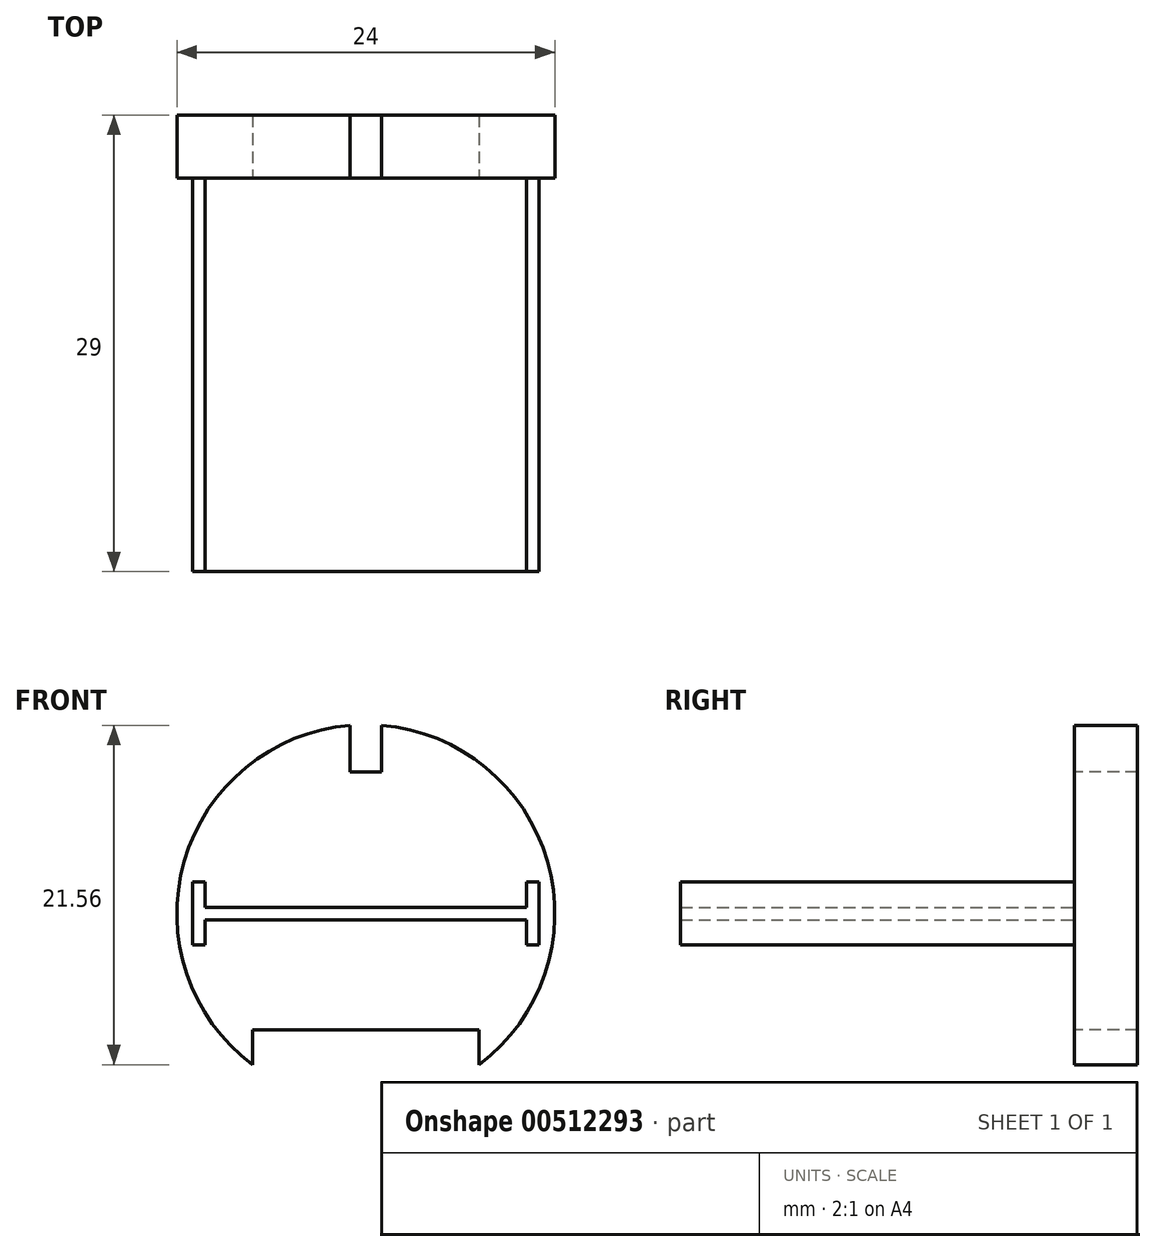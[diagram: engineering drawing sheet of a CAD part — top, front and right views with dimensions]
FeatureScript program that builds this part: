
annotation { "Feature Type Name" : "Feature", "Feature Type Description" : "" }
export const myFeature = defineFeature(function(context is Context, id is Id, definition is map)
    precondition{}
    {
        {
            var Q0;
            Q0=qCreatedBy(makeId("Front.planeOp"),FACE);
            var sketch = newSketch(context, id + "F0", { "sketchPlane" : qUnion([Q0])});
            skLineSegment(sketch, "E0.bottom", {"start": v(-10.2, 0.4) * mm, "end": v(10.2, 0.4) * mm});
            skLineSegment(sketch, "E0.top", {"start": v(-10.2, -0.4) * mm, "end": v(10.2, -0.4) * mm});
            skLineSegment(sketch, "E1", {"start": v(0, 0) * mm, "end": v(0, 72.24) * mm, "construction": true});
            skLineSegment(sketch, "E2", {"start": v(-29.5, 0) * mm, "end": v(0, 0) * mm, "construction": true});
            skLineSegment(sketch, "E3.bottom", {"start": v(-11, 2) * mm, "end": v(-10.2, 2) * mm});
            skLineSegment(sketch, "E3.top", {"start": v(-11, -2) * mm, "end": v(-10.2, -2) * mm});
            skLineSegment(sketch, "E3.left", {"start": v(-11, 2) * mm, "end": v(-11, -2) * mm});
            skLineSegment(sketch, "E3.right", {"start": v(-10.2, 2) * mm, "end": v(-10.2, 0.4) * mm});
            skLineSegment(sketch, "E4.bottom", {"start": v(11, 2) * mm, "end": v(10.2, 2) * mm});
            skLineSegment(sketch, "E4.top", {"start": v(11, -2) * mm, "end": v(10.2, -2) * mm});
            skLineSegment(sketch, "E4.left", {"start": v(11, 2) * mm, "end": v(11, -2) * mm});
            skLineSegment(sketch, "E4.right", {"start": v(10.2, 2) * mm, "end": v(10.2, 0.4) * mm});
            skLineSegment(sketch, "E5.trimOffspring", {"start": v(-10.2, -0.4) * mm, "end": v(-10.2, -2) * mm});
            skLineSegment(sketch, "E6.trimOffspring", {"start": v(10.2, -0.4) * mm, "end": v(10.2, -2) * mm});
            skPoint(sketch, "E7.trimOffspring.start.orphan", {"position": v(11, -0.4) * mm});
            skPoint(sketch, "E8.orphan", {"position": v(-11, 0.4) * mm});
            skLineSegment(sketch, "E9", {"start": v(10.2, -2) * mm, "end": v(-10.2, -2) * mm, "construction": true});
            skLineSegment(sketch, "E10", {"start": v(-10.2, 2) * mm, "end": v(10.2, 2) * mm, "construction": true});
            skSolve(sketch);
        }
        {
            var Q0;
            Q0=qCreatedBy(makeId("Front.planeOp"),FACE);
            var sketch = newSketch(context, id + "F1", { "sketchPlane" : qUnion([Q0])});
            skCircle(sketch, "E11", {"center": v(0, 0) * mm, "radius": 12 * mm});
            skSolve(sketch);
        }
        {
            var Q0;
            Q0 = qSketchRegion(id + "F1", true);
            extrude(context, id + "F2", {"entities" : qUnion([Q0]), "oppositeDirection" : true, "depth" : 4 * mm, "offsetDistance" : 25 * mm});
        }
        {
            var Q0;
            Q0 = qSketchRegion(id + "F0", true);
            extrude(context, id + "F3", {"entities" : qUnion([Q0]), "operationType" : NewBodyOperationType.ADD, "depth" : 25 * mm, "offsetDistance" : 25 * mm});
        }
        {
            var Q0;
            Q0=makeQuery(id+"F2.opExtrude","CAP_FACE",FACE,{"disambiguationData":[OSD([sQuery(id+"F1.wireOp",EDGE,"E11")])],"isStart":true});
            var sketch = newSketch(context, id + "F4", { "sketchPlane" : qUnion([Q0])});
            skLineSegment(sketch, "E12.bottom", {"start": v(-1, 14.62) * mm, "end": v(1, 14.62) * mm});
            skLineSegment(sketch, "E12.top", {"start": v(-1, 9) * mm, "end": v(1, 9) * mm});
            skLineSegment(sketch, "E12.left", {"start": v(-1, 14.62) * mm, "end": v(-1, 9) * mm});
            skLineSegment(sketch, "E12.right", {"start": v(1, 14.62) * mm, "end": v(1, 9) * mm});
            skLineSegment(sketch, "E13", {"start": v(0, 0) * mm, "end": v(0, 12) * mm, "construction": true});
            skLineSegment(sketch, "E14", {"start": v(-12, 0) * mm, "end": v(12, 0) * mm, "construction": true});
            skLineSegment(sketch, "E15.bottom", {"start": v(-7.2, -7.4) * mm, "end": v(7.2, -7.4) * mm});
            skLineSegment(sketch, "E15.top", {"start": v(-7.2, -17.4) * mm, "end": v(7.2, -17.4) * mm});
            skLineSegment(sketch, "E15.left", {"start": v(-7.2, -7.4) * mm, "end": v(-7.2, -17.4) * mm});
            skLineSegment(sketch, "E15.right", {"start": v(7.2, -7.4) * mm, "end": v(7.2, -17.4) * mm});
            skSolve(sketch);
        }
        {
            var Q0;
            Q0 = qSketchRegion(id + "F4", true);
            extrude(context, id + "F5", {"entities" : qUnion([Q0]), "operationType" : NewBodyOperationType.REMOVE, "endBound" : BoundingType.THROUGH_ALL, "oppositeDirection" : true, "depth" : 25 * mm, "offsetDistance" : 25 * mm});
        }
    });
